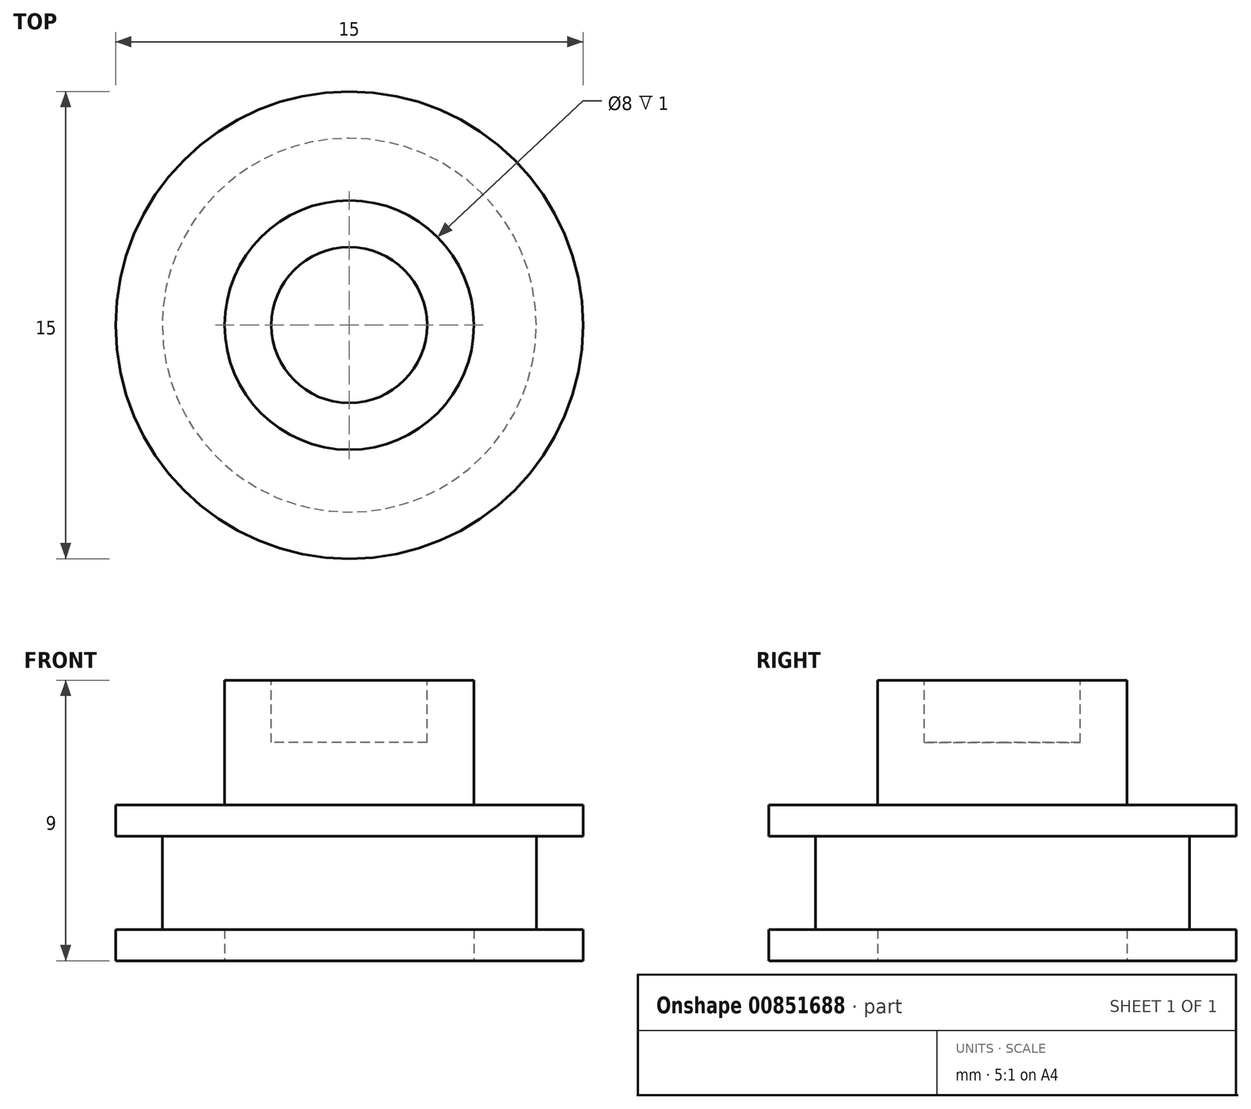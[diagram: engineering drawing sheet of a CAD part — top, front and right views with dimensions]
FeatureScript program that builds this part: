
annotation { "Feature Type Name" : "Feature", "Feature Type Description" : "" }
export const myFeature = defineFeature(function(context is Context, id is Id, definition is map)
    precondition{}
    {
        {
            var Q0;
            Q0=qCreatedBy(makeId("Top.planeOp"),FACE);
            var sketch = newSketch(context, id + "F0", { "sketchPlane" : qUnion([Q0])});
            skCircle(sketch, "E0", {"center": v(0, 0) * mm, "radius": 7.5 * mm});
            skSolve(sketch);
        }
        {
            var Q0;
            Q0=makeQuery(id+"F0.imprint","IMPRINT",FACE,{"disambiguationData":[TD([[makeQuery(id+"F0.imprint","IMPRINT",EDGE,{"derivedFrom":sQuery(id+"F0.wireOp",EDGE,"E0")}),1.0]])]});
            extrude(context, id + "F1", {"entities" : qUnion([Q0]), "depth" : 1 * mm, "offsetDistance" : 25 * mm});
        }
        {
            var Q0;
            Q0=makeQuery(id+"F1.opExtrude","CAP_FACE",FACE,{"disambiguationData":[OSD([sQuery(id+"F0.wireOp",EDGE,"E0")])],"isStart":false});
            var sketch = newSketch(context, id + "F2", { "sketchPlane" : qUnion([Q0])});
            skCircle(sketch, "E1", {"center": v(0, 0) * mm, "radius": 6 * mm});
            skSolve(sketch);
        }
        {
            var Q0;
            Q0=makeQuery(id+"F2.imprint","IMPRINT",FACE,{"disambiguationData":[TD([[makeQuery(id+"F2.imprint","IMPRINT",EDGE,{"derivedFrom":sQuery(id+"F2.wireOp",EDGE,"E1")}),1.0]])]});
            extrude(context, id + "F3", {"entities" : qUnion([Q0]), "operationType" : NewBodyOperationType.ADD, "depth" : 3 * mm, "offsetDistance" : 25 * mm});
        }
        {
            var Q0;
            Q0=makeQuery(id+"F3.opExtrude","CAP_FACE",FACE,{"disambiguationData":[OSD([sQuery(id+"F2.wireOp",EDGE,"E1")])],"isStart":false});
            var sketch = newSketch(context, id + "F4", { "sketchPlane" : qUnion([Q0])});
            skCircle(sketch, "E2", {"center": v(0, 0) * mm, "radius": 7.5 * mm});
            skSolve(sketch);
        }
        {
            var Q0;
            Q0=makeQuery(id+"F4.imprint","IMPRINT",FACE,{"disambiguationData":[TD([[makeQuery(id+"F4.imprint","IMPRINT",EDGE,{"derivedFrom":sQuery(id+"F4.wireOp",EDGE,"E2")}),1.0]])]});
            var Q1;
            Q1=makeQuery(id+"F4.imprint","IMPRINT",FACE,{"disambiguationData":[TD([[makeQuery(id+"F4.imprint","IMPRINT",EDGE,{"derivedFrom":makeQuery(id+"F3.opExtrude","CAP_EDGE",EDGE,{"disambiguationData":[OSD([sQuery(id+"F2.wireOp",EDGE,"E1")])],"isStart":false})}),1.0]])]});
            extrude(context, id + "F5", {"entities" : qUnion([Q0, Q1]), "operationType" : NewBodyOperationType.ADD, "depth" : 1 * mm, "offsetDistance" : 25 * mm});
        }
        {
            var Q0;
            Q0=makeQuery(id+"F5.opExtrude","CAP_FACE",FACE,{"disambiguationData":[OSD([sQuery(id+"F4.wireOp",EDGE,"E2")])],"isStart":false});
            var sketch = newSketch(context, id + "F6", { "sketchPlane" : qUnion([Q0])});
            skSolve(sketch);
        }
        {
            var Q0;
            Q0=makeQuery(id+"F6.imprint","IMPRINT",FACE,{"disambiguationData":[TD([[makeQuery(id+"F6.imprint","IMPRINT",EDGE,{"derivedFrom":makeQuery(id+"F5.opExtrude","CAP_EDGE",EDGE,{"disambiguationData":[OSD([sQuery(id+"F4.wireOp",EDGE,"E2")])],"isStart":false})}),1.0]])]});
            var sketch = newSketch(context, id + "F7", { "sketchPlane" : qUnion([Q0])});
            skCircle(sketch, "E3", {"center": v(0, 0) * mm, "radius": 4 * mm});
            skSolve(sketch);
        }
        {
            var Q0;
            Q0 = qSketchRegion(id + "F7", true);
            extrude(context, id + "F8", {"entities" : qUnion([Q0]), "operationType" : NewBodyOperationType.ADD, "depth" : 4 * mm, "offsetDistance" : 25 * mm});
        }
        {
            var Q0;
            Q0=makeQuery(id+"F8.opExtrude","CAP_FACE",FACE,{"disambiguationData":[OSD([sQuery(id+"F7.wireOp",EDGE,"E3")])],"isStart":false});
            var sketch = newSketch(context, id + "F9", { "sketchPlane" : qUnion([Q0])});
            skCircle(sketch, "E4", {"center": v(0, 0) * mm, "radius": 2.5 * mm});
            skSolve(sketch);
        }
        {
            var Q0;
            Q0=makeQuery(id+"F9.imprint","IMPRINT",FACE,{"disambiguationData":[TD([[makeQuery(id+"F9.imprint","IMPRINT",EDGE,{"derivedFrom":sQuery(id+"F9.wireOp",EDGE,"E4")}),1.0]])]});
            extrude(context, id + "F10", {"entities" : qUnion([Q0]), "operationType" : NewBodyOperationType.REMOVE, "oppositeDirection" : true, "depth" : 2 * mm, "offsetDistance" : 25 * mm});
        }
        {
            var Q0;
            Q0=makeQuery(id+"F1.opExtrude","CAP_FACE",FACE,{"disambiguationData":[OSD([sQuery(id+"F0.wireOp",EDGE,"E0")])],"isStart":true});
            var sketch = newSketch(context, id + "F11", { "sketchPlane" : qUnion([Q0])});
            skCircle(sketch, "E5", {"center": v(0, 0) * mm, "radius": 4 * mm});
            skSolve(sketch);
        }
        {
            var Q0;
            Q0=makeQuery(id+"F11.imprint","IMPRINT",FACE,{"disambiguationData":[TD([[makeQuery(id+"F11.imprint","IMPRINT",EDGE,{"derivedFrom":sQuery(id+"F11.wireOp",EDGE,"E5")}),1.0]])]});
            extrude(context, id + "F12", {"entities" : qUnion([Q0]), "operationType" : NewBodyOperationType.REMOVE, "oppositeDirection" : true, "depth" : 1 * mm, "offsetDistance" : 25 * mm});
        }
    });
